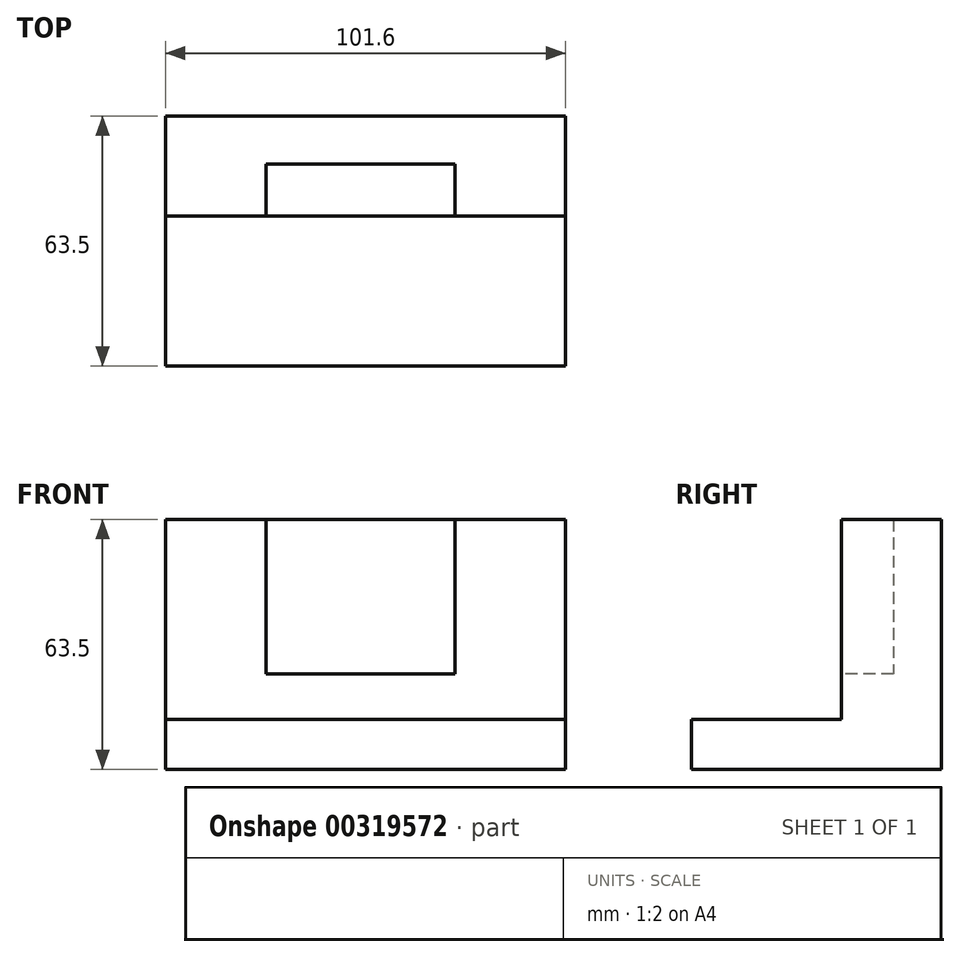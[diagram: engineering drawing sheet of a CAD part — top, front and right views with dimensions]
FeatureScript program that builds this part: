
annotation { "Feature Type Name" : "Feature", "Feature Type Description" : "" }
export const myFeature = defineFeature(function(context is Context, id is Id, definition is map)
    precondition{}
    {
        {
            var Q0;
            Q0=qCreatedBy(makeId("Right.planeOp"),FACE);
            var sketch = newSketch(context, id + "F0", { "sketchPlane" : qUnion([Q0])});
            skLineSegment(sketch, "E0", {"start": v(-28.33, -18.78) * mm, "end": v(-28.33, -31.48) * mm});
            skLineSegment(sketch, "E1", {"start": v(-28.33, -31.48) * mm, "end": v(35.17, -31.48) * mm});
            skLineSegment(sketch, "E2", {"start": v(35.17, -31.48) * mm, "end": v(35.17, 32.02) * mm});
            skLineSegment(sketch, "E3", {"start": v(35.17, 32.02) * mm, "end": v(9.77, 32.02) * mm});
            skLineSegment(sketch, "E4", {"start": v(9.77, 32.02) * mm, "end": v(9.77, -18.78) * mm});
            skLineSegment(sketch, "E5", {"start": v(9.77, -18.78) * mm, "end": v(-28.33, -18.78) * mm});
            skSolve(sketch);
        }
        {
            var Q0;
            Q0=makeQuery(id+"F0.imprint","IMPRINT",FACE,{"disambiguationData":[TD([[makeQuery(id+"F0.imprint","IMPRINT",EDGE,{"derivedFrom":sQuery(id+"F0.wireOp",EDGE,"E0")}),1.0]])]});
            extrude(context, id + "F1", {"entities" : qUnion([Q0]), "oppositeDirection" : true, "depth" : 101.6 * mm});
        }
        {
            var Q0;
            Q0=makeQuery(id+"F1.opExtrude","SWEPT_FACE",FACE,{"disambiguationData":[OSD([sQuery(id+"F0.wireOp",EDGE,"E4")])]});
            var sketch = newSketch(context, id + "F2", { "sketchPlane" : qUnion([Q0])});
            skLineSegment(sketch, "E6", {"start": v(-76.02, 32.02) * mm, "end": v(-76.02, -7.27) * mm});
            skLineSegment(sketch, "E7", {"start": v(-76.02, -7.27) * mm, "end": v(-28.1, -7.27) * mm});
            skLineSegment(sketch, "E8", {"start": v(-28.1, -7.27) * mm, "end": v(-28.1, 32.02) * mm});
            skSolve(sketch);
        }
        {
            var Q0;
            {var subQ0=sQuery(id+"F2.wireOp",EDGE,"E6");Q0=makeQuery(id+"F2.imprint","IMPRINT",FACE,{"disambiguationData":[TD([[makeQuery(id+"F2.imprint","IMPRINT",EDGE,{"derivedFrom":subQ0}),1.0]])]});}
            extrude(context, id + "F3", {"entities" : qUnion([Q0]), "operationType" : NewBodyOperationType.REMOVE, "oppositeDirection" : true, "depth" : 13.2 * mm});
        }
    });
